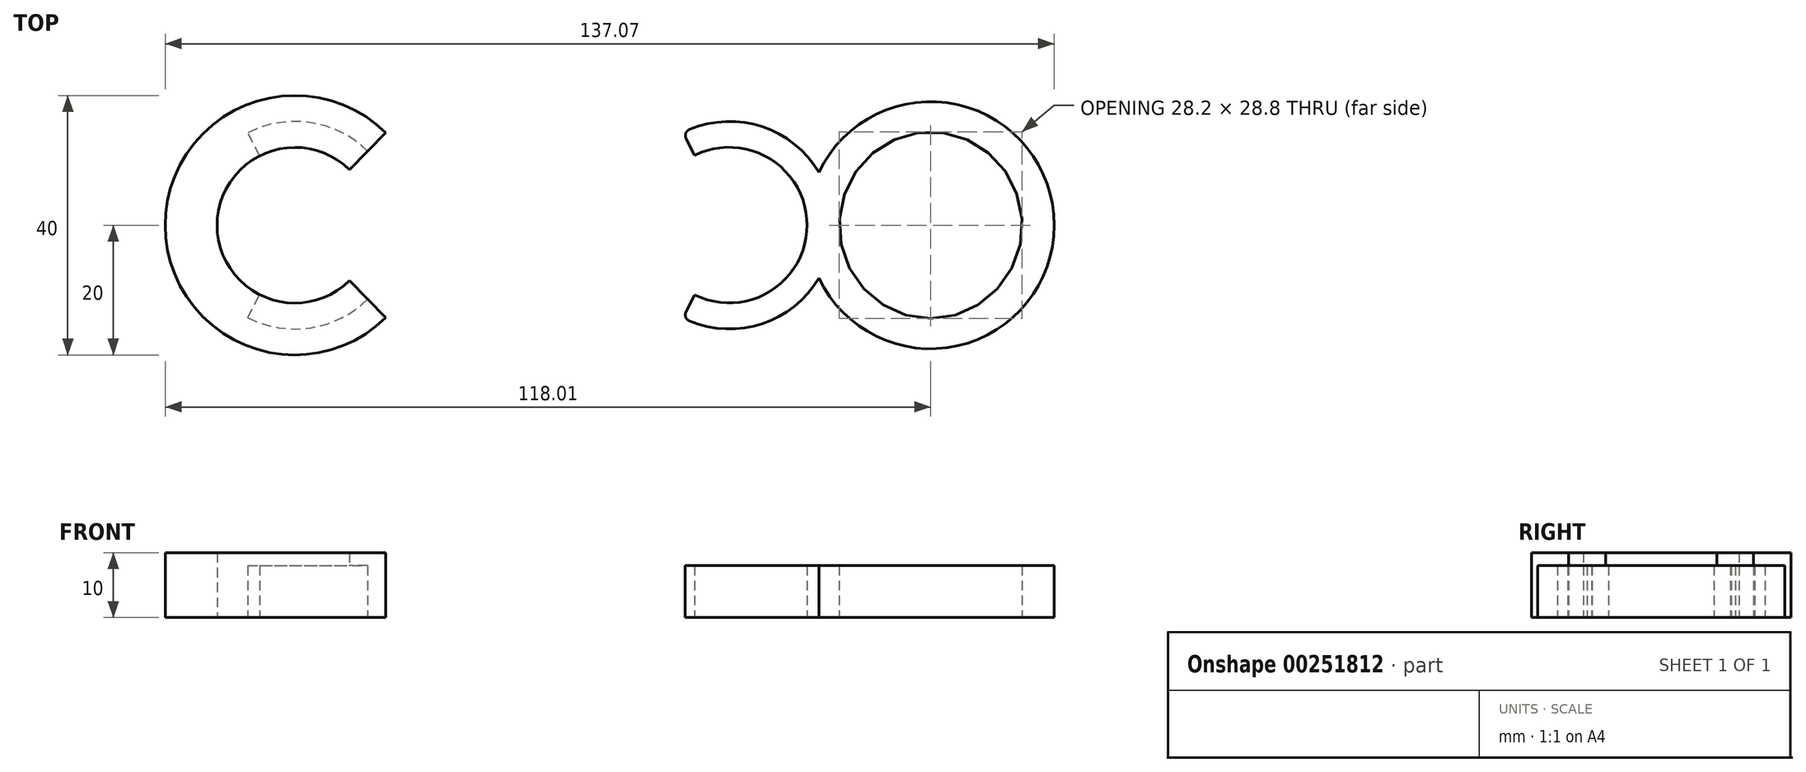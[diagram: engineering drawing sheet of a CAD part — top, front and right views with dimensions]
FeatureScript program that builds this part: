
annotation { "Feature Type Name" : "Feature", "Feature Type Description" : "" }
export const myFeature = defineFeature(function(context is Context, id is Id, definition is map)
    precondition{}
    {
        {
            var Q0;
            Q0=qCreatedBy(makeId("Top.planeOp"),FACE);
            var sketch = newSketch(context, id + "F0", { "sketchPlane" : qUnion([Q0])});
            skArc(sketch, "E0", {"start": v(-7.18, -14.3) * mm, "mid": v(16, 0) * mm, "end": v(-7.16, 14.3) * mm});
            skArc(sketch, "E1", {"start": v(-5.39, -10.73) * mm, "mid": v(11.94, 0.02) * mm, "end": v(-5.39, 10.77) * mm});
            skLineSegment(sketch, "E2", {"start": v(0, 0) * mm, "end": v(-9.86, 19.7) * mm, "construction": true});
            skLineSegment(sketch, "E3", {"start": v(0, 0) * mm, "end": v(-11.2, -22.32) * mm, "construction": true});
            skLineSegment(sketch, "E4", {"start": v(-5.39, 10.77) * mm, "end": v(-7.16, 14.3) * mm});
            skLineSegment(sketch, "E5", {"start": v(-5.39, -10.73) * mm, "end": v(-7.18, -14.3) * mm});
            skSolve(sketch);
        }
        {
            var Q0;
            Q0 = qSketchRegion(id + "F0", true);
            extrude(context, id + "F1", {"entities" : qUnion([Q0]), "depth" : 8 * mm});
        }
        {
            var Q0;
            Q0=qCreatedBy(makeId("Top.planeOp"),FACE);
            var sketch = newSketch(context, id + "F2", { "sketchPlane" : qUnion([Q0])});
            skCircle(sketch, "E6", {"center": v(31, 0) * mm, "radius": 19.06 * mm});
            skSolve(sketch);
        }
        {
            var Q0;
            Q0 = qSketchRegion(id + "F2", true);
            var Q1;
            Q1=makeQuery(id+"F1.opExtrude","CAP_FACE",FACE,{"disambiguationData":[OSD([sQuery(id+"F0.wireOp",EDGE,"E0"),sQuery(id+"F0.wireOp",EDGE,"E1"),sQuery(id+"F0.wireOp",EDGE,"E4"),sQuery(id+"F0.wireOp",EDGE,"E5")])],"isStart":false});
            extrude(context, id + "F3", {"entities" : qUnion([Q0]), "operationType" : NewBodyOperationType.ADD, "endBound" : BoundingType.UP_TO_SURFACE, "endBoundEntityFace" : qUnion([Q1]), "depth" : 25 * mm});
        }
        {
            var Q0;
            Q0=qCreatedBy(makeId("Top.planeOp"),FACE);
            var sketch = newSketch(context, id + "F4", { "sketchPlane" : qUnion([Q0])});
            skEllipse(sketch, "E7", {"center": v(31, 0) * mm, "majorRadius": 14.4 * mm, "minorRadius": 14.1 * mm, "majorAxis": v(0, -1)});
            skSolve(sketch);
        }
        {
            var Q0;
            Q0 = qSketchRegion(id + "F4", true);
            extrude(context, id + "F5", {"entities" : qUnion([Q0]), "operationType" : NewBodyOperationType.REMOVE, "endBound" : BoundingType.THROUGH_ALL, "depth" : 25 * mm});
        }
        {
            var Q0;
            Q0=makeQuery(id+"F1.opExtrude","SWEPT_EDGE",EDGE,{"disambiguationData":[OSD([sQuery(id+"F0.wireOp",EDGE,"E0"),sQuery(id+"F0.wireOp",EDGE,"E5")])]});
            var Q1;
            Q1=makeQuery(id+"F1.opExtrude","SWEPT_EDGE",EDGE,{"disambiguationData":[OSD([sQuery(id+"F0.wireOp",EDGE,"E0"),sQuery(id+"F0.wireOp",EDGE,"E4")])]});
            fillet(context, id + "F6", {"entities" : qUnion([Q0, Q1]), "radius" : 1 * mm, "tangentPropagation" : true, "allowEdgeOverflow" : false});
        }
        {
            var Q0;
            Q0=qCreatedBy(makeId("Top.planeOp"),FACE);
            var sketch = newSketch(context, id + "F7", { "sketchPlane" : qUnion([Q0])});
            skCircle(sketch, "E8", {"center": v(-67.01, 0) * mm, "radius": 20 * mm});
            skCircle(sketch, "E9", {"center": v(-67.01, 0) * mm, "radius": 12 * mm});
            skSolve(sketch);
        }
        {
            var Q0;
            Q0 = qSketchRegion(id + "F7", true);
            extrude(context, id + "F8", {"entities" : qUnion([Q0]), "depth" : 10 * mm});
        }
        {
            var Q0;
            Q0=qCreatedBy(makeId("Top.planeOp"),FACE);
            var sketch = newSketch(context, id + "F9", { "sketchPlane" : qUnion([Q0])});
            skArc(sketch, "E10", {"start": v(-74.28, -14.26) * mm, "mid": v(-51.01, 0) * mm, "end": v(-74.28, 14.26) * mm});
            skLineSegment(sketch, "E11", {"start": v(-67.01, 0) * mm, "end": v(-76.92, -19.45) * mm, "construction": true});
            skLineSegment(sketch, "E12", {"start": v(-67.01, 0) * mm, "end": v(-79.7, 24.9) * mm, "construction": true});
            skLineSegment(sketch, "E13", {"start": v(-74.28, -14.26) * mm, "end": v(-67.01, 0) * mm});
            skLineSegment(sketch, "E14", {"start": v(-67.01, 0) * mm, "end": v(-74.28, 14.26) * mm});
            skSolve(sketch);
        }
        {
            var Q0;
            Q0 = qSketchRegion(id + "F9", true);
            var Q1;
            Q1=makeQuery(id+"F3.boolean.opBoolean","MERGE",FACE,{"derivedFrom":[makeQuery(id+"F1.opExtrude","CAP_FACE",FACE,{"disambiguationData":[OSD([sQuery(id+"F0.wireOp",EDGE,"E0"),sQuery(id+"F0.wireOp",EDGE,"E1"),sQuery(id+"F0.wireOp",EDGE,"E4"),sQuery(id+"F0.wireOp",EDGE,"E5")])],"isStart":false}),makeQuery(id+"F3.opExtrude","CAP_FACE",FACE,{"disambiguationData":[OSD([sQuery(id+"F2.wireOp",EDGE,"E6")])],"isStart":false})]});
            extrude(context, id + "F10", {"entities" : qUnion([Q0]), "operationType" : NewBodyOperationType.REMOVE, "endBound" : BoundingType.UP_TO_SURFACE, "endBoundEntityFace" : qUnion([Q1]), "depth" : 25 * mm});
        }
        {
            var Q0;
            Q0=qCreatedBy(makeId("Top.planeOp"),FACE);
            var sketch = newSketch(context, id + "F11", { "sketchPlane" : qUnion([Q0])});
            skPoint(sketch, "E15", {"position": v(-52.99, -14.26) * mm});
            skPoint(sketch, "E16", {"position": v(-52.99, 14.26) * mm});
            skLineSegment(sketch, "E17", {"start": v(-67.01, 0) * mm, "end": v(-52.99, -14.26) * mm});
            skLineSegment(sketch, "E18", {"start": v(-67.01, 0) * mm, "end": v(-52.99, 14.26) * mm});
            skArc(sketch, "E19", {"start": v(-52.99, -14.26) * mm, "mid": v(-47.01, 0) * mm, "end": v(-52.99, 14.26) * mm});
            skSolve(sketch);
        }
        {
            var Q0;
            Q0 = qSketchRegion(id + "F11", true);
            extrude(context, id + "F12", {"entities" : qUnion([Q0]), "operationType" : NewBodyOperationType.REMOVE, "endBound" : BoundingType.THROUGH_ALL, "depth" : 25 * mm});
        }
    });
